# Revit family: Toilet-Floor_Mount-KOHLER-Reve-K-3797
name_source: partatom
category: Plumbing Fixtures
revit_build: Autodesk Revit 2015 (Build: 20140606_1530(x64)
units: mm (PartAtom-declared; Revit-internal decimal feet)

## types (3) — shared parameters
ADA Compliant = No
Assembly Code = D2010100
CW Connection = Yes
Cold Water Inlet = Cold Water Inlet
Date Modified = 07/31/2018
Default Elevation = 0"
Description = Comfort Height one-piece elongated dual-flush toilet with top actuator and skirted trapway
Flow Rate = 0 GPM
Flush Rate = 1.6 GPF
HW Connection = No
Height = 28"
Hot Water Inlet = Hot Water Inlet
Length = 27 1/4"
Manufacturer = KOHLER Co.
MasterFormat 1995 = 15410
MasterFormat 2004 = 22.41.13
Material = Vitreous china
Pressure = 0.00 psi
Product Documentation Link = http://www.us.kohler.com
Product Name = Reve
Product Page URL = http://www.us.kohler.com
Rough-In = 12"
Seat Included = Yes
URL = https://www.us.kohler.com
Vent Connection = No
Waste Connection = Yes
Waste Water Outlet = Waste Water Outlet
Width = 14 1/2"

## per-type parameters (varying)
| type | Finish | Model | Type |
| 0-White | Kohler-Vitreous_China-0-White | K-3797-0 | 1 |
| 96-Biscuit | Kohler-Vitreous_China-96-Biscuit | K-3797-96 | 2 |
| 47-Almond | Kohler-Vitreous_China-47-Almond | K-3797-47 | 3 |

## geometry (parser evidence)
native form markers: Blend x2, Sweep x4
no freeform markers — native parametric forms only
